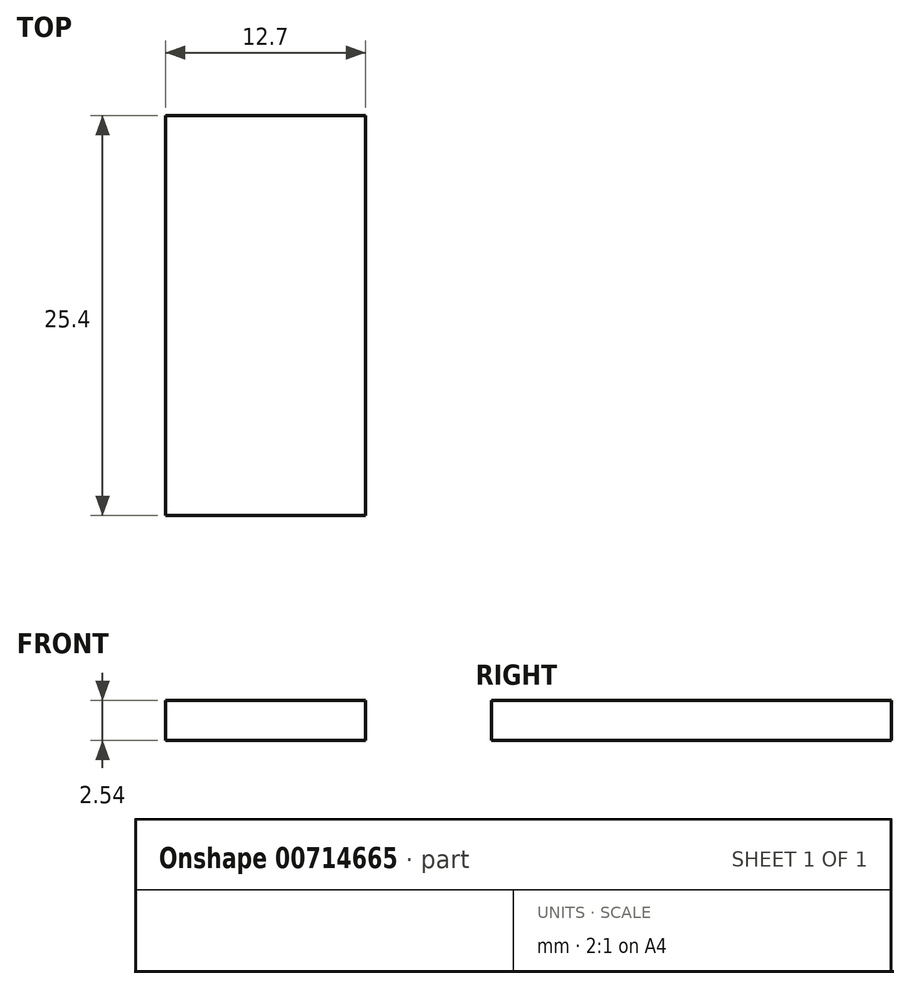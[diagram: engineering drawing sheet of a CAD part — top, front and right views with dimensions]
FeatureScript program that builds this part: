
annotation { "Feature Type Name" : "Feature", "Feature Type Description" : "" }
export const myFeature = defineFeature(function(context is Context, id is Id, definition is map)
    precondition{}
    {
        {
            var Q0;
            Q0=qCreatedBy(makeId("Top.planeOp"),FACE);
            var sketch = newSketch(context, id + "F0", { "sketchPlane" : qUnion([Q0])});
            skLineSegment(sketch, "E0.bottom", {"start": v(0, 0) * mm, "end": v(12.7, 0) * mm});
            skLineSegment(sketch, "E0.top", {"start": v(0, 25.4) * mm, "end": v(12.7, 25.4) * mm});
            skLineSegment(sketch, "E0.left", {"start": v(0, 0) * mm, "end": v(0, 25.4) * mm});
            skLineSegment(sketch, "E0.right", {"start": v(12.7, 0) * mm, "end": v(12.7, 25.4) * mm});
            skSolve(sketch);
        }
        {
            var Q0;
            Q0=makeQuery(id+"F0.imprint","IMPRINT",FACE,{"disambiguationData":[TD([[makeQuery(id+"F0.imprint","IMPRINT",EDGE,{"derivedFrom":sQuery(id+"F0.wireOp",EDGE,"E0.bottom")}),1.0]])]});
            extrude(context, id + "F1", {"entities" : qUnion([Q0]), "depth" : 2.54 * mm, "offsetDistance" : 25.4 * mm});
        }
    });
